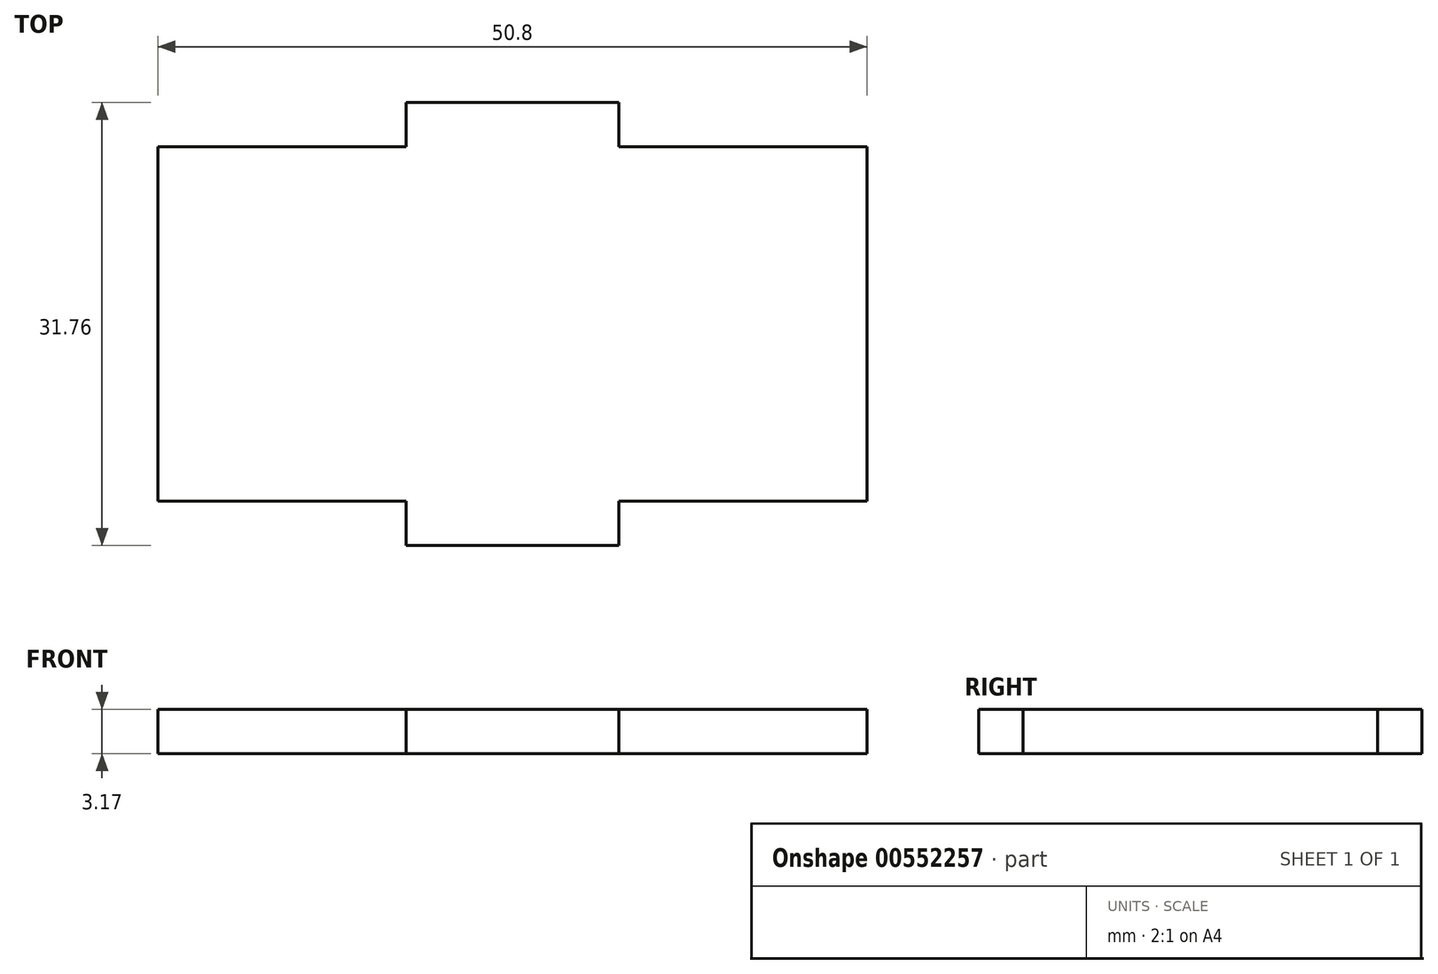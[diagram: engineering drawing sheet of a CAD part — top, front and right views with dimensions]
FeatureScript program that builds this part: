
annotation { "Feature Type Name" : "Feature", "Feature Type Description" : "" }
export const myFeature = defineFeature(function(context is Context, id is Id, definition is map)
    precondition{}
    {
        {
            var Q0;
            Q0=qCreatedBy(makeId("Top.planeOp"),FACE);
            var sketch = newSketch(context, id + "F0", { "sketchPlane" : qUnion([Q0])});
            skPoint(sketch, "E0.middle", {"position": v(0, 0) * mm});
            skLineSegment(sketch, "E1", {"start": v(0, 15.88) * mm, "end": v(7.62, 15.88) * mm});
            skLineSegment(sketch, "E2", {"start": v(0, 15.88) * mm, "end": v(-7.62, 15.88) * mm});
            skLineSegment(sketch, "E3", {"start": v(-7.62, -15.88) * mm, "end": v(0, -15.88) * mm});
            skLineSegment(sketch, "E4", {"start": v(-7.62, 15.88) * mm, "end": v(-7.62, 12.7) * mm});
            skLineSegment(sketch, "E5", {"start": v(-7.62, 12.7) * mm, "end": v(-12.7, 12.7) * mm});
            skLineSegment(sketch, "E6", {"start": v(7.62, 15.88) * mm, "end": v(7.62, 12.7) * mm});
            skLineSegment(sketch, "E7", {"start": v(7.62, 12.7) * mm, "end": v(12.7, 12.7) * mm});
            skLineSegment(sketch, "E8", {"start": v(0, -15.88) * mm, "end": v(7.62, -15.88) * mm});
            skLineSegment(sketch, "E9", {"start": v(12.7, -12.7) * mm, "end": v(7.62, -12.7) * mm});
            skLineSegment(sketch, "E10", {"start": v(7.62, -12.7) * mm, "end": v(7.62, -15.88) * mm});
            skLineSegment(sketch, "E11", {"start": v(-7.62, -15.88) * mm, "end": v(-7.62, -12.7) * mm});
            skLineSegment(sketch, "E12", {"start": v(-7.62, -12.7) * mm, "end": v(-12.7, -12.7) * mm});
            skLineSegment(sketch, "E13", {"start": v(-12.7, 12.7) * mm, "end": v(-25.4, 12.7) * mm});
            skLineSegment(sketch, "E14", {"start": v(-25.4, 12.7) * mm, "end": v(-25.4, 0) * mm});
            skLineSegment(sketch, "E15", {"start": v(25.4, 0) * mm, "end": v(25.4, -12.7) * mm});
            skLineSegment(sketch, "E16.bottom", {"start": v(-25.4, 12.7) * mm, "end": v(25.4, 12.7) * mm});
            skLineSegment(sketch, "E16.top", {"start": v(-25.4, -12.7) * mm, "end": v(25.4, -12.7) * mm});
            skLineSegment(sketch, "E16.left", {"start": v(-25.4, 12.7) * mm, "end": v(-25.4, -12.7) * mm});
            skLineSegment(sketch, "E16.right", {"start": v(25.4, 12.7) * mm, "end": v(25.4, -12.7) * mm});
            skSolve(sketch);
        }
        {
            var Q0;
            Q0 = qSketchRegion(id + "F0", true);
            extrude(context, id + "F1", {"entities" : qUnion([Q0]), "depth" : 3.17 * mm, "offsetDistance" : 25.4 * mm});
        }
    });
